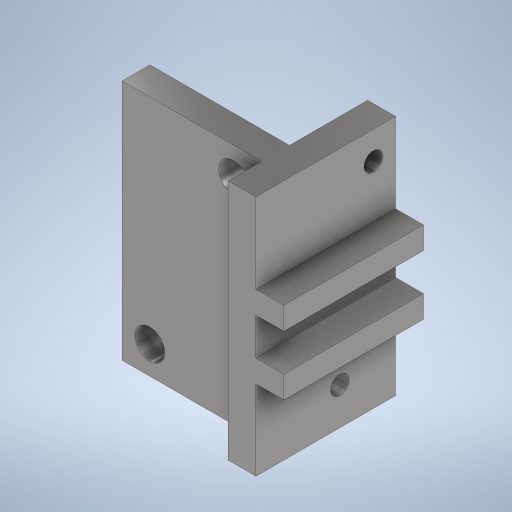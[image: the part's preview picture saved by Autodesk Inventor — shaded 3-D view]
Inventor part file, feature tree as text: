
AUTODESK INVENTOR PART (.ipt)
format: ipt  version: 2024 (Build 280153000, 153)  size: 303,104 bytes
history: native  units: mm
features: sketch x8, extrude x4, hole x3, plane x1, mirror x1
ambient origin geometry x8: Origin, YZ Plane, XZ Plane, XY Plane, X Axis, Y Axis, Z Axis, Center Point
bodies: Volumenkörper1 (feature_tree)
feature tree (17):
  extrude  "Extrusion1"  Depth=75.0mm
  extrude  "Extrusion2"  Depth=15.0mm
  plane  "Arbeitsebene1"
  extrude  "Extrusion3"  Depth=75.0mm TaperAngle=0.0deg
  extrude  "Extrusion4"  TaperAngle=45.0deg  [1 undecoded]
  mirror  "Spiegeln1"
  hole  "Bohrung1"  [1 undecoded]
  hole  "Bohrung3"  [1 undecoded]
  hole  "Bohrung4"  [1 undecoded]
  sketch  "Skizze1"  dims[d0=15.0mm d1=75.0mm]
  sketch  "Skizze2"  dims[d2=130.0mm d3=0.0mm d4=15.0mm]
  sketch  "Skizze4"  dims[d5=18.0mm d6=75.0mm d7=0.0mm]
  sketch  "Skizze5"  dims[d8=65.0mm d9=45.0deg]
  sketch  "Skizze6"  dims[d10=12.0mm d11=0.0mm d12=12.0mm]
  sketch  "Skizze7"  dims[d13=10.0mm d14=75.0mm]
  sketch  "Skizze8"  dims[d15=15.0mm d16=0.0mm]
  sketch  "Skizze9"  dims[d17=10.0mm d18=6.0mm d19=4.0mm d20=2.0mm d21=90.0deg d22=8.0mm d23=0.0mm d24=30.0mm d25=20.0mm d26=10.0mm d27=6.0mm d28=4.0mm d29=2.0mm d30=90.0deg d31=8.0mm d32=0.0mm d33=30.0mm d34=15.0mm d35=16.0mm d36=6.0mm d37=4.0mm d38=2.0mm d39=90.0deg d40=8.0mm d41=0.0mm d42=15.0mm d43=15.0mm d44=16.0mm d45=6.0mm d46=4.0mm d47=2.0mm d48=90.0deg d49=8.0mm d50=0.0mm d51=15.0mm d52=15.0mm]
note: 4 required parameter values undecoded (feature->parameter linkage not recoverable at this tier; creation-order binding heuristic only, values carry confidence <= 0.55)
